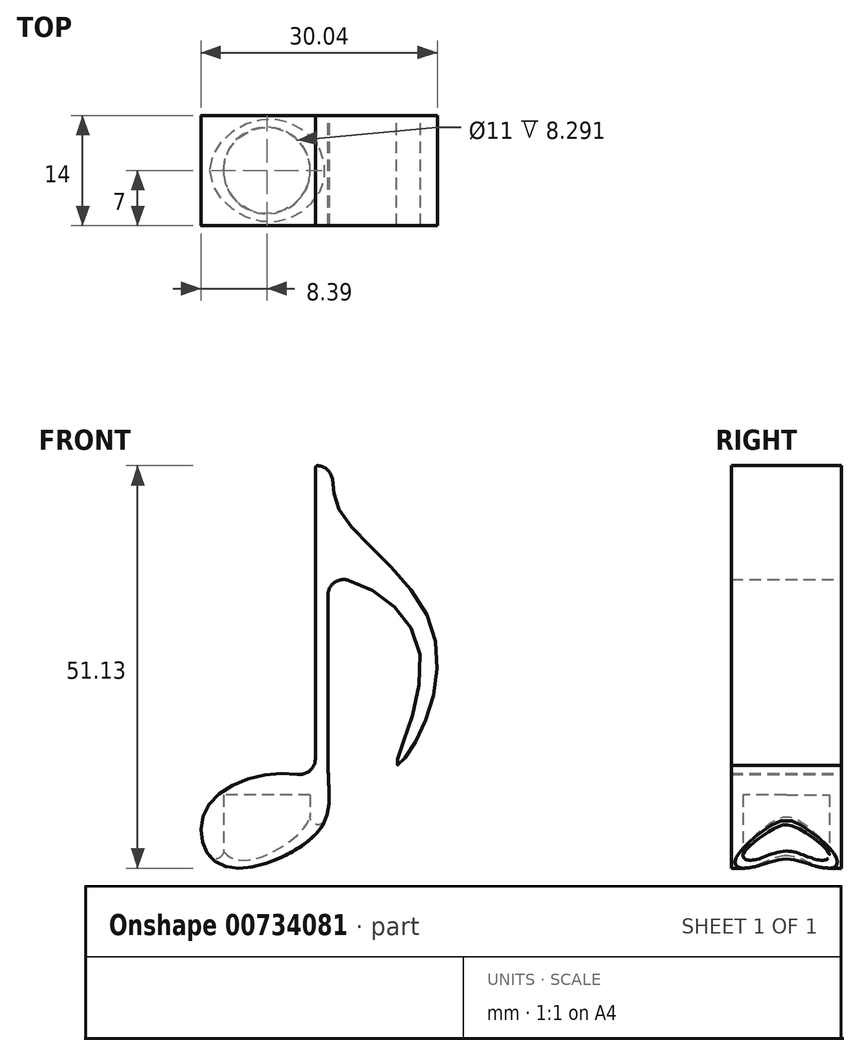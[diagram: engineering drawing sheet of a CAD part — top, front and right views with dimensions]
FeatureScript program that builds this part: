
annotation { "Feature Type Name" : "Feature", "Feature Type Description" : "" }
export const myFeature = defineFeature(function(context is Context, id is Id, definition is map)
    precondition{}
    {
        {
            var Q0;
            Q0=qCreatedBy(makeId("Top.planeOp"),FACE);
            var sketch = newSketch(context, id + "F0", { "sketchPlane" : qUnion([Q0])});
            skCircle(sketch, "E0", {"center": v(0, 0) * mm, "radius": 5.5 * mm});
            skSolve(sketch);
        }
        {
            var Q0;
            Q0 = qSketchRegion(id + "F0", true);
            extrude(context, id + "F1", {"entities" : qUnion([Q0]), "depth" : 154.7 * mm, "offsetDistance" : 25 * mm});
        }
        {
            var Q0;
            Q0=qCreatedBy(makeId("Front.planeOp"),FACE);
            var sketch = newSketch(context, id + "F2", { "sketchPlane" : qUnion([Q0])});
            skFitSpline(sketch, "E1", {"points": [v(6.16, 156.54) * mm, v(-7.23, 153.68) * mm, v(-6.05, 145.94) * mm, v(5.4, 148.97) * mm, v(7.75, 156.63) * mm], "startDerivative": vector(-33.3, 20.7) * mm, "endDerivative": vector(-6.94, 49.4) * mm});
            skLineSegment(sketch, "E2", {"start": v(7.75, 156.63) * mm, "end": v(7.75, 180.07) * mm});
            skFitSpline(sketch, "E3", {"points": [v(7.75, 182.51) * mm, v(19.39, 172.91) * mm, v(16.47, 158.56) * mm, v(18.76, 161.26) * mm, v(20.62, 176.92) * mm, v(9.1, 191.08) * mm, v(7.75, 196.54) * mm], "startDerivative": vector(69.57, -6.3) * mm, "endDerivative": vector(-25.18, 43.4) * mm});
            skLineSegment(sketch, "E4", {"start": v(6.34, 196.54) * mm, "end": v(6.16, 196.54) * mm});
            skLineSegment(sketch, "E5", {"start": v(6.16, 196.54) * mm, "end": v(6.16, 159.31) * mm});
            skArc(sketch, "E6.filletArc", {"start": v(3.85, 157.34) * mm, "mid": v(5.46, 157.8) * mm, "end": v(6.16, 159.31) * mm});
            skArc(sketch, "E7.filletArc", {"start": v(10.34, 181.98) * mm, "mid": v(8.57, 181.68) * mm, "end": v(7.75, 180.07) * mm});
            skArc(sketch, "E8.filletArc", {"start": v(8.31, 194.84) * mm, "mid": v(7.64, 196.06) * mm, "end": v(6.34, 196.54) * mm});
            skSolve(sketch);
        }
        {
            var Q0;
            Q0 = qSketchRegion(id + "F2", true);
            extrude(context, id + "F3", {"entities" : qUnion([Q0]), "depth" : 7 * mm, "offsetDistance" : 25 * mm, "hasSecondDirection" : true, "secondDirectionOppositeDirection" : true, "secondDirectionDepth" : 7 * mm});
        }
        {
            var Q0;
            Q0=makeQuery(id+"F3.opExtrude","SWEPT_EDGE",EDGE,{"disambiguationData":[OSD([sQuery(id+"F2.wireOp",EDGE,"E4"),sQuery(id+"F2.wireOp",EDGE,"E5")])]});
            fillet(context, id + "F4", {"entities" : qUnion([Q0]), "radius" : 0.3 * mm, "tangentPropagation" : true, "allowEdgeOverflow" : false});
        }
        {
            var Q0;
            Q0=makeQuery(id+"F3.opExtrude","SWEPT_EDGE",EDGE,{"disambiguationData":[OSD([sQuery(id+"F2.wireOp",EDGE,"E1"),sQuery(id+"F2.wireOp",EDGE,"E2")])]});
            fillet(context, id + "F5", {"entities" : qUnion([Q0]), "radius" : 81.87 * mm, "tangentPropagation" : true, "allowEdgeOverflow" : false});
        }
        {
            var Q0;
            Q0=makeQuery(id+"F1.opExtrude","SWEPT_BODY",BODY,{"disambiguationData":[OSD([sQuery(id+"F0.wireOp",EDGE,"E0")])]});
            var Q1;
            Q1=makeQuery(id+"F3.opExtrude","SWEPT_BODY",BODY,{"disambiguationData":[OSD([sQuery(id+"F2.wireOp",EDGE,"E1"),sQuery(id+"F2.wireOp",EDGE,"E2"),sQuery(id+"F2.wireOp",EDGE,"E3"),sQuery(id+"F2.wireOp",EDGE,"E4"),sQuery(id+"F2.wireOp",EDGE,"E5"),sQuery(id+"F2.wireOp",EDGE,"E6.filletArc"),sQuery(id+"F2.wireOp",EDGE,"E7.filletArc"),sQuery(id+"F2.wireOp",EDGE,"E8.filletArc")])]});
            booleanBodies(context, id + "F6", {"operationType" : BooleanOperationType.SUBTRACTION, "tools" : qUnion([Q0]), "targets" : qUnion([Q1])});
        }
        {
            var Q0;
            Q0=makeQuery(id+"F6.opBoolean","INTERSECT",EDGE,{"derivedFrom":[makeQuery(id+"F1.opExtrude","SWEPT_FACE",FACE,{"disambiguationData":[OSD([sQuery(id+"F0.wireOp",EDGE,"E0")])]}),makeQuery(id+"F3.opExtrude","SWEPT_FACE",FACE,{"disambiguationData":[OSD([sQuery(id+"F2.wireOp",EDGE,"E1")])]})]});
            fillet(context, id + "F7", {"entities" : qUnion([Q0]), "radius" : 1 * mm, "tangentPropagation" : true, "allowEdgeOverflow" : false});
        }
    });
